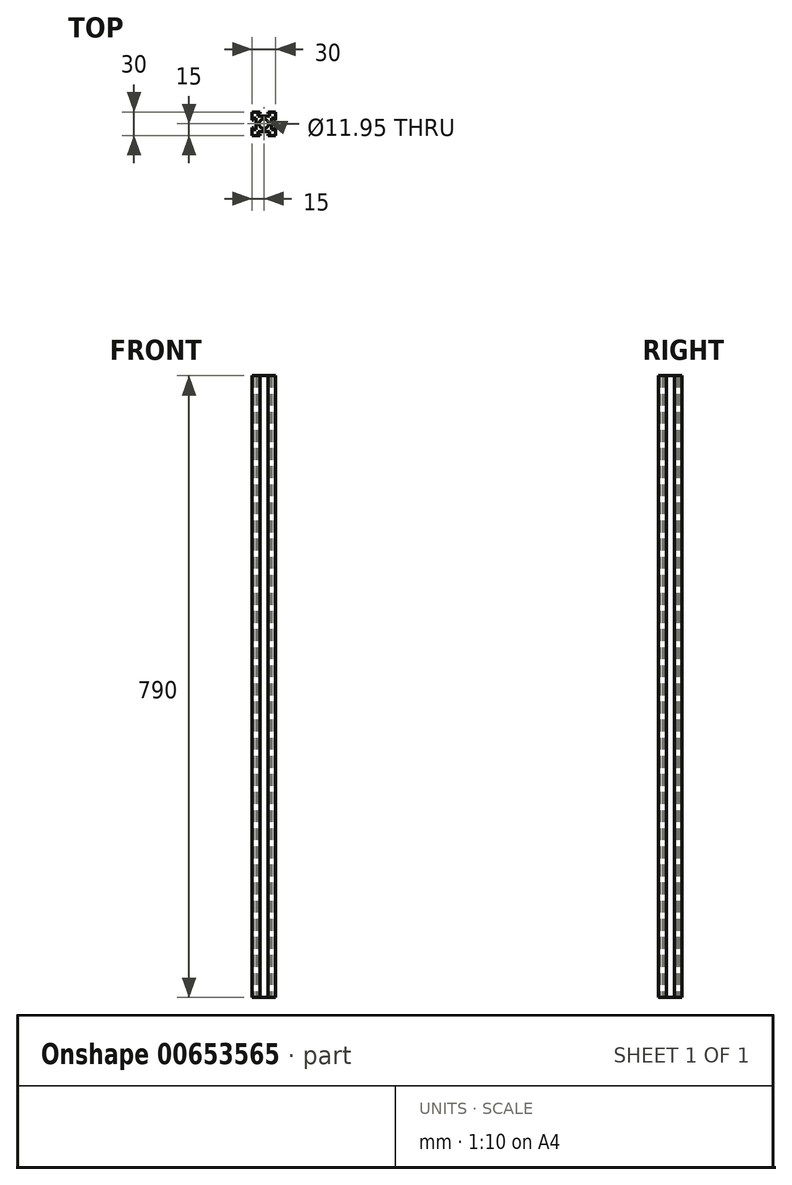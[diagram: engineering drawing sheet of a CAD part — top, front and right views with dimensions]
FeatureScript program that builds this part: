
annotation { "Feature Type Name" : "Feature", "Feature Type Description" : "" }
export const myFeature = defineFeature(function(context is Context, id is Id, definition is map)
    precondition{}
    {
        {
            var Q0;
            Q0=qCreatedBy(makeId("Top.planeOp"),FACE);
            var sketch = newSketch(context, id + "F0", { "sketchPlane" : qUnion([Q0])});
            skLineSegment(sketch, "E0.top", {"start": v(5, 15) * mm, "end": v(15, 15) * mm});
            skLineSegment(sketch, "E0.right", {"start": v(15, 5) * mm, "end": v(15, 15) * mm});
            skLineSegment(sketch, "E1", {"start": v(5, 15) * mm, "end": v(5, 13) * mm});
            skLineSegment(sketch, "E2", {"start": v(5, 13) * mm, "end": v(7.5, 13) * mm});
            skLineSegment(sketch, "E3", {"start": v(7.5, 13) * mm, "end": v(7.5, 10) * mm});
            skLineSegment(sketch, "E4", {"start": v(7.5, 10) * mm, "end": v(0, 10) * mm});
            skLineSegment(sketch, "E5", {"start": v(15, 5) * mm, "end": v(13, 5) * mm});
            skLineSegment(sketch, "E6", {"start": v(13, 5) * mm, "end": v(13, 7.5) * mm});
            skLineSegment(sketch, "E7", {"start": v(13, 7.5) * mm, "end": v(10, 7.5) * mm});
            skLineSegment(sketch, "E8", {"start": v(10, 7.5) * mm, "end": v(10, 0) * mm});
            skLineSegment(sketch, "E9.1.0", {"start": v(-5, 15) * mm, "end": v(-5, 13) * mm});
            skLineSegment(sketch, "E9.1.1", {"start": v(-7.5, 13) * mm, "end": v(-7.5, 10) * mm});
            skLineSegment(sketch, "E9.1.3", {"start": v(-5, 13) * mm, "end": v(-7.5, 13) * mm});
            skLineSegment(sketch, "E9.1.5", {"start": v(-5, 15) * mm, "end": v(-15, 15) * mm});
            skLineSegment(sketch, "E9.1.7", {"start": v(-13, 5) * mm, "end": v(-13, 7.5) * mm});
            skLineSegment(sketch, "E9.1.9", {"start": v(-15, 5) * mm, "end": v(-15, 15) * mm});
            skLineSegment(sketch, "E9.1.10", {"start": v(-13, 7.5) * mm, "end": v(-10, 7.5) * mm});
            skLineSegment(sketch, "E9.1.11", {"start": v(-15, 5) * mm, "end": v(-13, 5) * mm});
            skLineSegment(sketch, "E9.1.12", {"start": v(-10, 7.5) * mm, "end": v(-10, 0) * mm});
            skLineSegment(sketch, "E9.1.14", {"start": v(-7.5, 10) * mm, "end": v(0, 10) * mm});
            skLineSegment(sketch, "E9.1.16", {"start": v(-7.5, 10) * mm, "end": v(0, 10) * mm});
            skLineSegment(sketch, "E9.1.17", {"start": v(-5, 13) * mm, "end": v(-7.5, 13) * mm});
            skLineSegment(sketch, "E9.1.19", {"start": v(-10, 7.5) * mm, "end": v(-10, 0) * mm});
            skLineSegment(sketch, "E9.1.20", {"start": v(-5, 15) * mm, "end": v(-15, 15) * mm});
            skLineSegment(sketch, "E9.1.21", {"start": v(-13, 5) * mm, "end": v(-13, 7.5) * mm});
            skLineSegment(sketch, "E9.1.22", {"start": v(-15, 5) * mm, "end": v(-13, 5) * mm});
            skLineSegment(sketch, "E9.1.23", {"start": v(-5, 15) * mm, "end": v(-5, 13) * mm});
            skLineSegment(sketch, "E9.1.24", {"start": v(-15, 5) * mm, "end": v(-15, 15) * mm});
            skLineSegment(sketch, "E9.1.26", {"start": v(-13, 7.5) * mm, "end": v(-10, 7.5) * mm});
            skLineSegment(sketch, "E9.1.28", {"start": v(-7.5, 13) * mm, "end": v(-7.5, 10) * mm});
            skLineSegment(sketch, "E9.1.29", {"start": v(-5, 15) * mm, "end": v(-5, 13) * mm});
            skLineSegment(sketch, "E9.1.30", {"start": v(-5, 15) * mm, "end": v(-15, 15) * mm});
            skLineSegment(sketch, "E9.1.32", {"start": v(-15, 5) * mm, "end": v(-15, 15) * mm});
            skLineSegment(sketch, "E9.1.33", {"start": v(-15, 5) * mm, "end": v(-13, 5) * mm});
            skLineSegment(sketch, "E9.1.34", {"start": v(-13, 5) * mm, "end": v(-13, 7.5) * mm});
            skLineSegment(sketch, "E9.1.35", {"start": v(-10, 7.5) * mm, "end": v(-10, 0) * mm});
            skLineSegment(sketch, "E9.1.36", {"start": v(-13, 7.5) * mm, "end": v(-10, 7.5) * mm});
            skLineSegment(sketch, "E9.1.37", {"start": v(-5, 13) * mm, "end": v(-7.5, 13) * mm});
            skLineSegment(sketch, "E9.1.39", {"start": v(-7.5, 10) * mm, "end": v(0, 10) * mm});
            skLineSegment(sketch, "E9.1.40", {"start": v(-7.5, 13) * mm, "end": v(-7.5, 10) * mm});
            skLineSegment(sketch, "E9.1.41", {"start": v(-7.5, 10) * mm, "end": v(0, 10) * mm});
            skLineSegment(sketch, "E9.1.42", {"start": v(-13, 5) * mm, "end": v(-13, 7.5) * mm});
            skLineSegment(sketch, "E9.1.44", {"start": v(-13, 7.5) * mm, "end": v(-10, 7.5) * mm});
            skLineSegment(sketch, "E9.1.45", {"start": v(-5, 15) * mm, "end": v(-15, 15) * mm});
            skLineSegment(sketch, "E9.1.46", {"start": v(-5, 13) * mm, "end": v(-7.5, 13) * mm});
            skLineSegment(sketch, "E9.1.47", {"start": v(-15, 5) * mm, "end": v(-15, 15) * mm});
            skLineSegment(sketch, "E9.1.48", {"start": v(-15, 5) * mm, "end": v(-13, 5) * mm});
            skLineSegment(sketch, "E9.1.49", {"start": v(-7.5, 13) * mm, "end": v(-7.5, 10) * mm});
            skLineSegment(sketch, "E9.1.50", {"start": v(-10, 7.5) * mm, "end": v(-10, 0) * mm});
            skLineSegment(sketch, "E9.1.51", {"start": v(-5, 15) * mm, "end": v(-5, 13) * mm});
            skLineSegment(sketch, "E9.2.0", {"start": v(-15, -5) * mm, "end": v(-13, -5) * mm});
            skLineSegment(sketch, "E9.2.1", {"start": v(-13, -7.5) * mm, "end": v(-10, -7.5) * mm});
            skLineSegment(sketch, "E9.2.3", {"start": v(-13, -5) * mm, "end": v(-13, -7.5) * mm});
            skLineSegment(sketch, "E9.2.5", {"start": v(-15, -5) * mm, "end": v(-15, -15) * mm});
            skPoint(sketch, "E9.2.6", {"position": v(0, 0) * mm});
            skLineSegment(sketch, "E9.2.7", {"start": v(-5, -13) * mm, "end": v(-7.5, -13) * mm});
            skLineSegment(sketch, "E9.2.9", {"start": v(-5, -15) * mm, "end": v(-15, -15) * mm});
            skLineSegment(sketch, "E9.2.10", {"start": v(-7.5, -13) * mm, "end": v(-7.5, -10) * mm});
            skLineSegment(sketch, "E9.2.11", {"start": v(-5, -15) * mm, "end": v(-5, -13) * mm});
            skLineSegment(sketch, "E9.2.12", {"start": v(-7.5, -10) * mm, "end": v(0, -10) * mm});
            skLineSegment(sketch, "E9.2.14", {"start": v(-10, -7.5) * mm, "end": v(-10, 0) * mm});
            skLineSegment(sketch, "E9.2.16", {"start": v(-10, -7.5) * mm, "end": v(-10, 0) * mm});
            skLineSegment(sketch, "E9.2.17", {"start": v(-13, -5) * mm, "end": v(-13, -7.5) * mm});
            skLineSegment(sketch, "E9.2.19", {"start": v(-7.5, -10) * mm, "end": v(0, -10) * mm});
            skLineSegment(sketch, "E9.2.20", {"start": v(-15, -5) * mm, "end": v(-15, -15) * mm});
            skLineSegment(sketch, "E9.2.21", {"start": v(-5, -13) * mm, "end": v(-7.5, -13) * mm});
            skLineSegment(sketch, "E9.2.22", {"start": v(-5, -15) * mm, "end": v(-5, -13) * mm});
            skLineSegment(sketch, "E9.2.23", {"start": v(-15, -5) * mm, "end": v(-13, -5) * mm});
            skLineSegment(sketch, "E9.2.24", {"start": v(-5, -15) * mm, "end": v(-15, -15) * mm});
            skLineSegment(sketch, "E9.2.26", {"start": v(-7.5, -13) * mm, "end": v(-7.5, -10) * mm});
            skLineSegment(sketch, "E9.2.28", {"start": v(-13, -7.5) * mm, "end": v(-10, -7.5) * mm});
            skLineSegment(sketch, "E9.2.29", {"start": v(-15, -5) * mm, "end": v(-13, -5) * mm});
            skLineSegment(sketch, "E9.2.30", {"start": v(-15, -5) * mm, "end": v(-15, -15) * mm});
            skLineSegment(sketch, "E9.2.32", {"start": v(-5, -15) * mm, "end": v(-15, -15) * mm});
            skLineSegment(sketch, "E9.2.33", {"start": v(-5, -15) * mm, "end": v(-5, -13) * mm});
            skLineSegment(sketch, "E9.2.34", {"start": v(-5, -13) * mm, "end": v(-7.5, -13) * mm});
            skLineSegment(sketch, "E9.2.35", {"start": v(-7.5, -10) * mm, "end": v(0, -10) * mm});
            skLineSegment(sketch, "E9.2.36", {"start": v(-7.5, -13) * mm, "end": v(-7.5, -10) * mm});
            skLineSegment(sketch, "E9.2.37", {"start": v(-13, -5) * mm, "end": v(-13, -7.5) * mm});
            skLineSegment(sketch, "E9.2.39", {"start": v(-10, -7.5) * mm, "end": v(-10, 0) * mm});
            skLineSegment(sketch, "E9.2.40", {"start": v(-13, -7.5) * mm, "end": v(-10, -7.5) * mm});
            skLineSegment(sketch, "E9.2.41", {"start": v(-10, -7.5) * mm, "end": v(-10, 0) * mm});
            skLineSegment(sketch, "E9.2.42", {"start": v(-5, -13) * mm, "end": v(-7.5, -13) * mm});
            skLineSegment(sketch, "E9.2.44", {"start": v(-7.5, -13) * mm, "end": v(-7.5, -10) * mm});
            skLineSegment(sketch, "E9.2.45", {"start": v(-15, -5) * mm, "end": v(-15, -15) * mm});
            skLineSegment(sketch, "E9.2.46", {"start": v(-13, -5) * mm, "end": v(-13, -7.5) * mm});
            skLineSegment(sketch, "E9.2.47", {"start": v(-5, -15) * mm, "end": v(-15, -15) * mm});
            skLineSegment(sketch, "E9.2.48", {"start": v(-5, -15) * mm, "end": v(-5, -13) * mm});
            skLineSegment(sketch, "E9.2.49", {"start": v(-13, -7.5) * mm, "end": v(-10, -7.5) * mm});
            skLineSegment(sketch, "E9.2.50", {"start": v(-7.5, -10) * mm, "end": v(0, -10) * mm});
            skLineSegment(sketch, "E9.2.51", {"start": v(-15, -5) * mm, "end": v(-13, -5) * mm});
            skLineSegment(sketch, "E9.3.0", {"start": v(5, -15) * mm, "end": v(5, -13) * mm});
            skLineSegment(sketch, "E9.3.1", {"start": v(7.5, -13) * mm, "end": v(7.5, -10) * mm});
            skLineSegment(sketch, "E9.3.3", {"start": v(5, -13) * mm, "end": v(7.5, -13) * mm});
            skLineSegment(sketch, "E9.3.5", {"start": v(5, -15) * mm, "end": v(15, -15) * mm});
            skLineSegment(sketch, "E9.3.7", {"start": v(13, -5) * mm, "end": v(13, -7.5) * mm});
            skLineSegment(sketch, "E9.3.9", {"start": v(15, -5) * mm, "end": v(15, -15) * mm});
            skLineSegment(sketch, "E9.3.10", {"start": v(13, -7.5) * mm, "end": v(10, -7.5) * mm});
            skLineSegment(sketch, "E9.3.11", {"start": v(15, -5) * mm, "end": v(13, -5) * mm});
            skLineSegment(sketch, "E9.3.12", {"start": v(10, -7.5) * mm, "end": v(10, 0) * mm});
            skLineSegment(sketch, "E9.3.14", {"start": v(7.5, -10) * mm, "end": v(0, -10) * mm});
            skLineSegment(sketch, "E9.3.16", {"start": v(7.5, -10) * mm, "end": v(0, -10) * mm});
            skLineSegment(sketch, "E9.3.17", {"start": v(5, -13) * mm, "end": v(7.5, -13) * mm});
            skLineSegment(sketch, "E9.3.19", {"start": v(10, -7.5) * mm, "end": v(10, 0) * mm});
            skLineSegment(sketch, "E9.3.20", {"start": v(5, -15) * mm, "end": v(15, -15) * mm});
            skLineSegment(sketch, "E9.3.21", {"start": v(13, -5) * mm, "end": v(13, -7.5) * mm});
            skLineSegment(sketch, "E9.3.22", {"start": v(15, -5) * mm, "end": v(13, -5) * mm});
            skLineSegment(sketch, "E9.3.23", {"start": v(5, -15) * mm, "end": v(5, -13) * mm});
            skLineSegment(sketch, "E9.3.24", {"start": v(15, -5) * mm, "end": v(15, -15) * mm});
            skLineSegment(sketch, "E9.3.26", {"start": v(13, -7.5) * mm, "end": v(10, -7.5) * mm});
            skLineSegment(sketch, "E9.3.28", {"start": v(7.5, -13) * mm, "end": v(7.5, -10) * mm});
            skLineSegment(sketch, "E9.3.29", {"start": v(5, -15) * mm, "end": v(5, -13) * mm});
            skLineSegment(sketch, "E9.3.30", {"start": v(5, -15) * mm, "end": v(15, -15) * mm});
            skLineSegment(sketch, "E9.3.32", {"start": v(15, -5) * mm, "end": v(15, -15) * mm});
            skLineSegment(sketch, "E9.3.33", {"start": v(15, -5) * mm, "end": v(13, -5) * mm});
            skLineSegment(sketch, "E9.3.34", {"start": v(13, -5) * mm, "end": v(13, -7.5) * mm});
            skLineSegment(sketch, "E9.3.35", {"start": v(10, -7.5) * mm, "end": v(10, 0) * mm});
            skLineSegment(sketch, "E9.3.36", {"start": v(13, -7.5) * mm, "end": v(10, -7.5) * mm});
            skLineSegment(sketch, "E9.3.37", {"start": v(5, -13) * mm, "end": v(7.5, -13) * mm});
            skLineSegment(sketch, "E9.3.39", {"start": v(7.5, -10) * mm, "end": v(0, -10) * mm});
            skLineSegment(sketch, "E9.3.40", {"start": v(7.5, -13) * mm, "end": v(7.5, -10) * mm});
            skLineSegment(sketch, "E9.3.41", {"start": v(7.5, -10) * mm, "end": v(0, -10) * mm});
            skLineSegment(sketch, "E9.3.42", {"start": v(13, -5) * mm, "end": v(13, -7.5) * mm});
            skLineSegment(sketch, "E9.3.44", {"start": v(13, -7.5) * mm, "end": v(10, -7.5) * mm});
            skLineSegment(sketch, "E9.3.45", {"start": v(5, -15) * mm, "end": v(15, -15) * mm});
            skLineSegment(sketch, "E9.3.46", {"start": v(5, -13) * mm, "end": v(7.5, -13) * mm});
            skLineSegment(sketch, "E9.3.47", {"start": v(15, -5) * mm, "end": v(15, -15) * mm});
            skLineSegment(sketch, "E9.3.48", {"start": v(15, -5) * mm, "end": v(13, -5) * mm});
            skLineSegment(sketch, "E9.3.49", {"start": v(7.5, -13) * mm, "end": v(7.5, -10) * mm});
            skLineSegment(sketch, "E9.3.50", {"start": v(10, -7.5) * mm, "end": v(10, 0) * mm});
            skLineSegment(sketch, "E9.3.51", {"start": v(5, -15) * mm, "end": v(5, -13) * mm});
            skCircle(sketch, "E10", {"center": v(0, 0) * mm, "radius": 5.98 * mm});
            skSolve(sketch);
        }
        {
            var Q0;
            Q0 = qSketchRegion(id + "F0", true);
            extrude(context, id + "F1", {"entities" : qUnion([Q0]), "depth" : 790 * mm, "offsetDistance" : 25 * mm});
        }
    });
